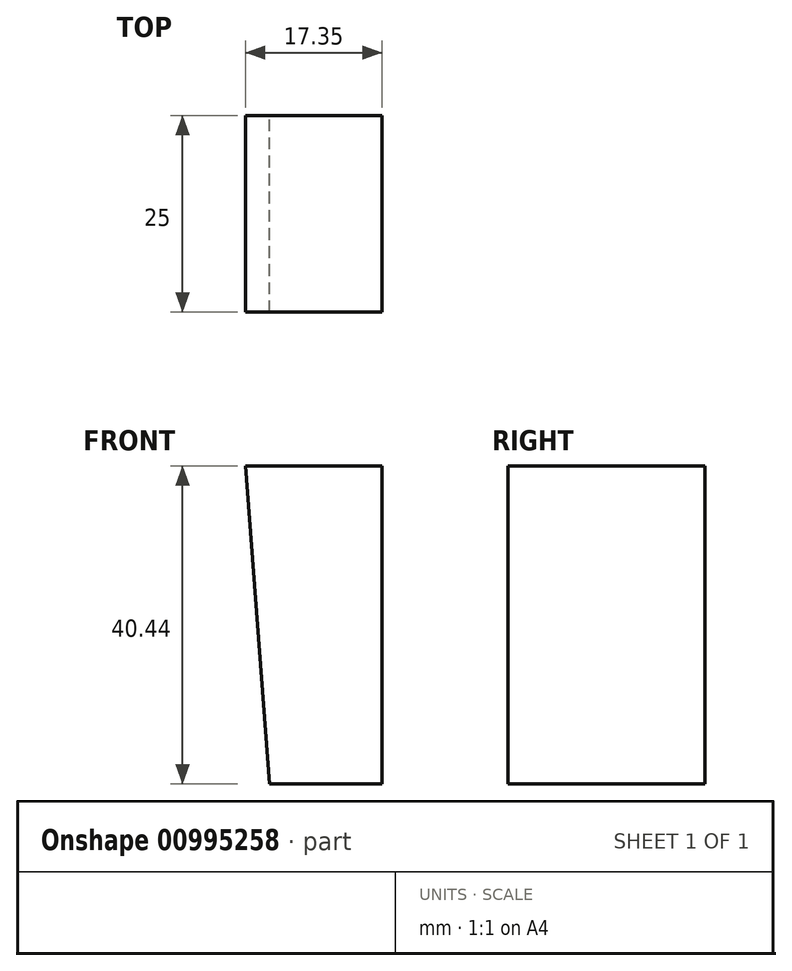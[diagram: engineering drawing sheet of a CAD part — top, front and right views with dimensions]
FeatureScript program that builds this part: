
annotation { "Feature Type Name" : "Feature", "Feature Type Description" : "" }
export const myFeature = defineFeature(function(context is Context, id is Id, definition is map)
    precondition{}
    {
        {
            var Q0;
            Q0=qCreatedBy(makeId("Front.planeOp"),FACE);
            var sketch = newSketch(context, id + "F0", { "sketchPlane" : qUnion([Q0])});
            skLineSegment(sketch, "E0", {"start": v(-73.75, 8.57) * mm, "end": v(-59.46, 8.57) * mm});
            skLineSegment(sketch, "E1", {"start": v(-59.46, 8.57) * mm, "end": v(-59.46, 49) * mm});
            skLineSegment(sketch, "E2", {"start": v(-59.46, 49) * mm, "end": v(-76.8, 49) * mm});
            skLineSegment(sketch, "E3", {"start": v(-76.8, 49) * mm, "end": v(-73.75, 8.57) * mm});
            skSolve(sketch);
        }
        {
            var Q0;
            Q0=makeQuery(id+"F0.imprint","IMPRINT",FACE,{"disambiguationData":[TD([[makeQuery(id+"F0.imprint","IMPRINT",EDGE,{"derivedFrom":sQuery(id+"F0.wireOp",EDGE,"E0")}),1.0]])]});
            extrude(context, id + "F1", {"entities" : qUnion([Q0]), "depth" : 25 * mm, "offsetDistance" : 25 * mm});
        }
    });
